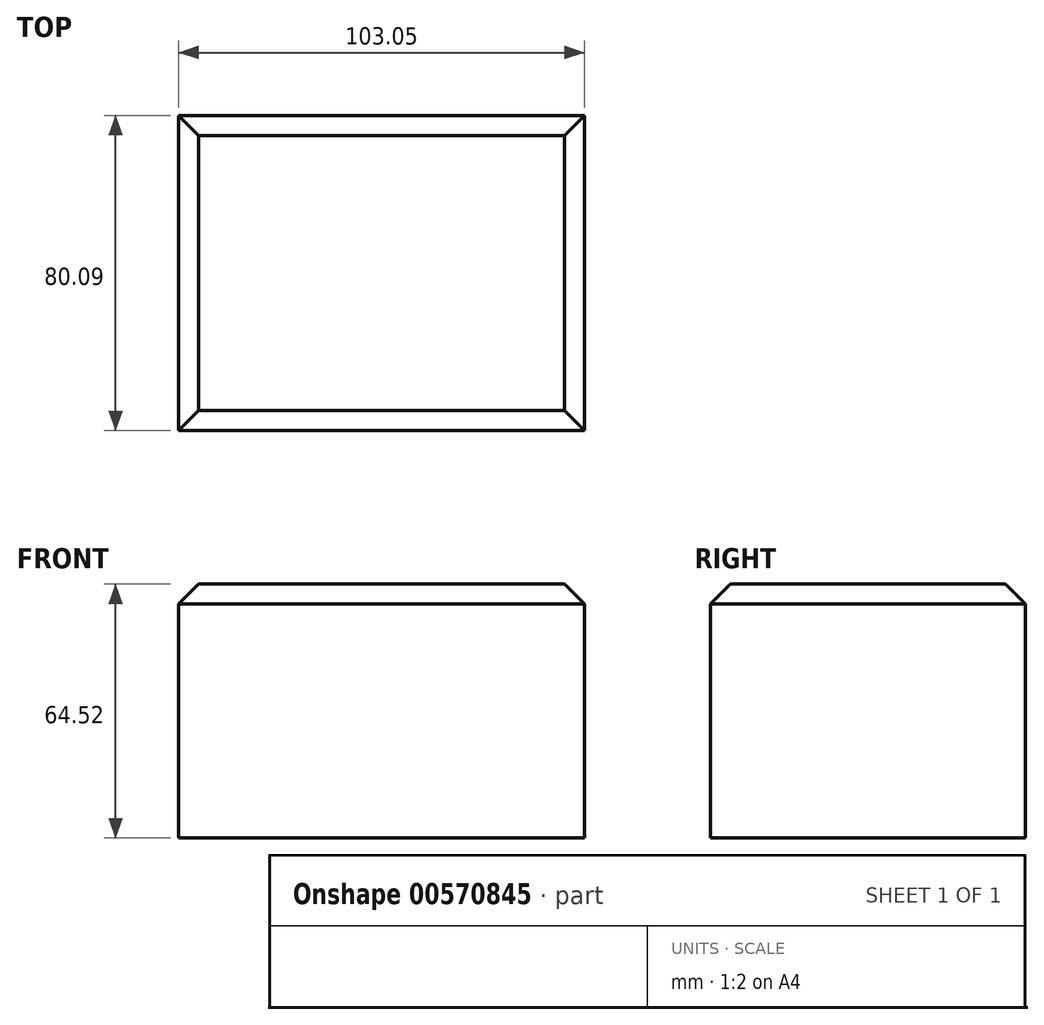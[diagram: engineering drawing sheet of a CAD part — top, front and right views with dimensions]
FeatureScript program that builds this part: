
annotation { "Feature Type Name" : "Feature", "Feature Type Description" : "" }
export const myFeature = defineFeature(function(context is Context, id is Id, definition is map)
    precondition{}
    {
        {
            var Q0;
            Q0=qCreatedBy(makeId("Top.planeOp"),FACE);
            var sketch = newSketch(context, id + "F0", { "sketchPlane" : qUnion([Q0])});
            skLineSegment(sketch, "E0.bottom", {"start": v(-51.91, -40.27) * mm, "end": v(51.14, -40.27) * mm});
            skLineSegment(sketch, "E0.top", {"start": v(-51.91, 39.82) * mm, "end": v(51.14, 39.82) * mm});
            skLineSegment(sketch, "E0.left", {"start": v(-51.91, -40.27) * mm, "end": v(-51.91, 39.82) * mm});
            skLineSegment(sketch, "E0.right", {"start": v(51.14, -40.27) * mm, "end": v(51.14, 39.82) * mm});
            skSolve(sketch);
        }
        {
            var Q0;
            Q0=makeQuery(id+"F0.imprint","IMPRINT",FACE,{"disambiguationData":[TD([[makeQuery(id+"F0.imprint","IMPRINT",EDGE,{"derivedFrom":sQuery(id+"F0.wireOp",EDGE,"E0.bottom")}),1.0]])]});
            extrude(context, id + "F1", {"entities" : qUnion([Q0]), "depth" : 64.52 * mm, "offsetDistance" : 25.4 * mm});
        }
        {
            var Q0;
            Q0=makeQuery(id+"F1.opExtrude","CAP_EDGE",EDGE,{"disambiguationData":[OSD([sQuery(id+"F0.wireOp",EDGE,"E0.bottom")])],"isStart":false});
            var Q1;
            Q1=makeQuery(id+"F1.opExtrude","CAP_EDGE",EDGE,{"disambiguationData":[OSD([sQuery(id+"F0.wireOp",EDGE,"E0.right")])],"isStart":false});
            var Q2;
            Q2=makeQuery(id+"F1.opExtrude","CAP_EDGE",EDGE,{"disambiguationData":[OSD([sQuery(id+"F0.wireOp",EDGE,"E0.top")])],"isStart":false});
            var Q3;
            Q3=makeQuery(id+"F1.opExtrude","CAP_FACE",FACE,{"disambiguationData":[OSD([sQuery(id+"F0.wireOp",EDGE,"E0.bottom"),sQuery(id+"F0.wireOp",EDGE,"E0.top"),sQuery(id+"F0.wireOp",EDGE,"E0.left"),sQuery(id+"F0.wireOp",EDGE,"E0.right")])],"isStart":false});
            chamfer(context, id + "F2", {"entities" : qUnion([Q0, Q1, Q2, Q3]), "width" : 5.08 * mm, "tangentPropagation" : true});
        }
    });
